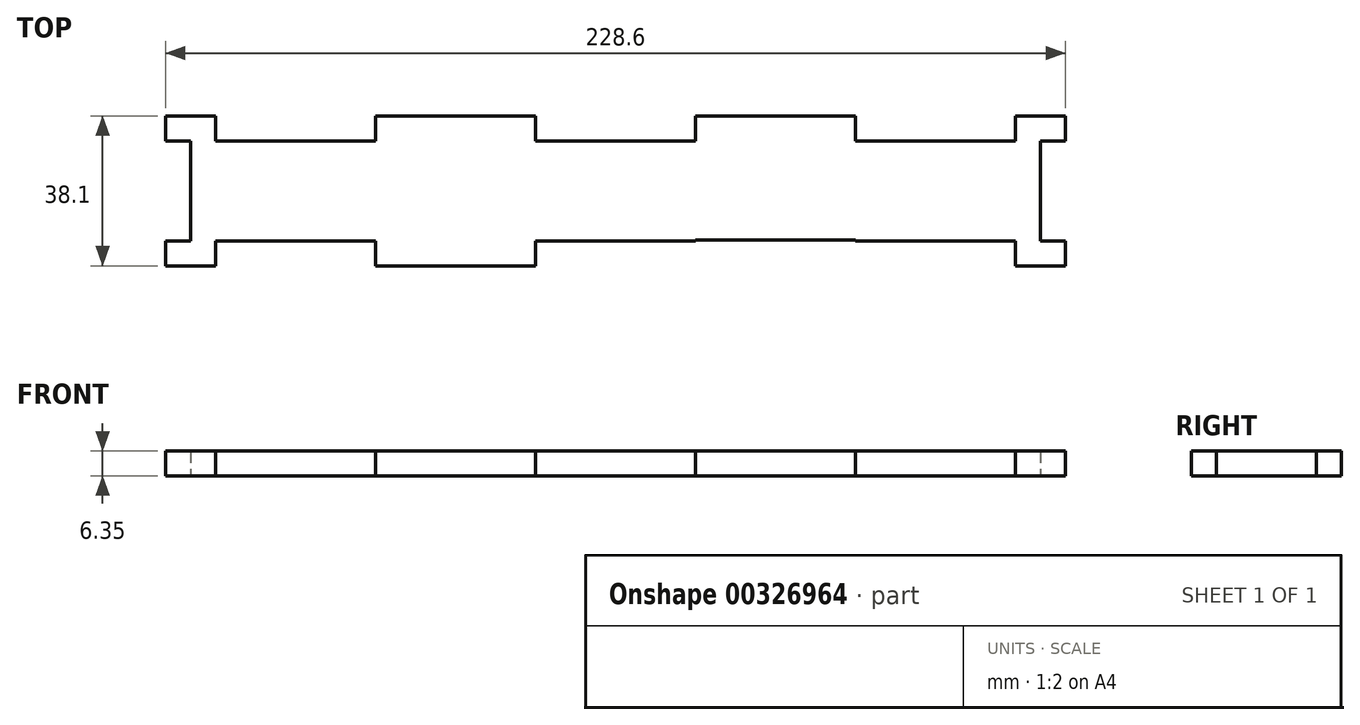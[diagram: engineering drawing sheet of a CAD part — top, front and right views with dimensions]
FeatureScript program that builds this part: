
annotation { "Feature Type Name" : "Feature", "Feature Type Description" : "" }
export const myFeature = defineFeature(function(context is Context, id is Id, definition is map)
    precondition{}
    {
        {
            var Q0;
            Q0=qCreatedBy(makeId("Top.planeOp"),FACE);
            var sketch = newSketch(context, id + "F0", { "sketchPlane" : qUnion([Q0])});
            skLineSegment(sketch, "E0.bottom", {"start": v(-114.3, 19.05) * mm, "end": v(114.3, 19.05) * mm});
            skLineSegment(sketch, "E0.top", {"start": v(-114.3, -19.05) * mm, "end": v(114.3, -19.05) * mm});
            skLineSegment(sketch, "E0.left", {"start": v(-114.3, 19.05) * mm, "end": v(-114.3, -19.05) * mm});
            skLineSegment(sketch, "E0.right", {"start": v(114.3, 19.05) * mm, "end": v(114.3, -19.05) * mm});
            skPoint(sketch, "E0.middle", {"position": v(0, 0) * mm});
            skLineSegment(sketch, "E1", {"start": v(-114.3, 19.05) * mm, "end": v(-114.3, 12.7) * mm});
            skLineSegment(sketch, "E2.bottom", {"start": v(-114.3, 12.7) * mm, "end": v(-107.95, 12.7) * mm});
            skLineSegment(sketch, "E2.top", {"start": v(-114.3, -12.7) * mm, "end": v(-107.95, -12.7) * mm});
            skLineSegment(sketch, "E2.left", {"start": v(-114.3, 12.7) * mm, "end": v(-114.3, -12.7) * mm});
            skLineSegment(sketch, "E2.right", {"start": v(-107.95, 12.7) * mm, "end": v(-107.95, -12.7) * mm});
            skLineSegment(sketch, "E3", {"start": v(-114.3, 19.05) * mm, "end": v(-101.6, 19.05) * mm});
            skLineSegment(sketch, "E4.bottom", {"start": v(-101.6, 19.05) * mm, "end": v(-60.96, 19.05) * mm});
            skLineSegment(sketch, "E4.top", {"start": v(-101.6, 12.7) * mm, "end": v(-60.96, 12.7) * mm});
            skLineSegment(sketch, "E4.left", {"start": v(-101.6, 19.05) * mm, "end": v(-101.6, 12.7) * mm});
            skLineSegment(sketch, "E4.right", {"start": v(-60.96, 19.05) * mm, "end": v(-60.96, 12.7) * mm});
            skLineSegment(sketch, "E5", {"start": v(-60.96, 19.05) * mm, "end": v(-20.32, 19.05) * mm});
            skLineSegment(sketch, "E6.bottom", {"start": v(-20.32, 19.05) * mm, "end": v(20.32, 19.05) * mm});
            skLineSegment(sketch, "E6.top", {"start": v(-20.32, 12.7) * mm, "end": v(20.32, 12.7) * mm});
            skLineSegment(sketch, "E6.left", {"start": v(-20.32, 19.05) * mm, "end": v(-20.32, 12.7) * mm});
            skLineSegment(sketch, "E6.right", {"start": v(20.32, 19.05) * mm, "end": v(20.32, 12.7) * mm});
            skLineSegment(sketch, "E7", {"start": v(20.32, 19.05) * mm, "end": v(38.62, 19.05) * mm});
            skLineSegment(sketch, "E8", {"start": v(114.3, 19.05) * mm, "end": v(101.6, 19.05) * mm});
            skLineSegment(sketch, "E9.bottom", {"start": v(101.6, 19.05) * mm, "end": v(60.96, 19.05) * mm});
            skLineSegment(sketch, "E9.top", {"start": v(101.6, 12.7) * mm, "end": v(60.96, 12.7) * mm});
            skLineSegment(sketch, "E9.left", {"start": v(101.6, 19.05) * mm, "end": v(101.6, 12.7) * mm});
            skLineSegment(sketch, "E9.right", {"start": v(60.96, 19.05) * mm, "end": v(60.96, 12.7) * mm});
            skLineSegment(sketch, "E10", {"start": v(-114.3, -19.05) * mm, "end": v(-101.6, -19.05) * mm});
            skLineSegment(sketch, "E11.bottom", {"start": v(-101.6, -19.05) * mm, "end": v(-60.96, -19.05) * mm});
            skLineSegment(sketch, "E11.top", {"start": v(-101.6, -12.7) * mm, "end": v(-60.96, -12.7) * mm});
            skLineSegment(sketch, "E11.left", {"start": v(-101.6, -19.05) * mm, "end": v(-101.6, -12.7) * mm});
            skLineSegment(sketch, "E11.right", {"start": v(-60.96, -19.05) * mm, "end": v(-60.96, -12.7) * mm});
            skLineSegment(sketch, "E12", {"start": v(-60.96, -19.05) * mm, "end": v(-39.72, -19.05) * mm});
            skLineSegment(sketch, "E13", {"start": v(114.3, -19.05) * mm, "end": v(101.6, -19.05) * mm});
            skLineSegment(sketch, "E14.bottom", {"start": v(101.6, -19.05) * mm, "end": v(60.96, -19.05) * mm});
            skLineSegment(sketch, "E14.top", {"start": v(101.6, -12.7) * mm, "end": v(60.96, -12.7) * mm});
            skLineSegment(sketch, "E14.left", {"start": v(101.6, -19.05) * mm, "end": v(101.6, -12.7) * mm});
            skLineSegment(sketch, "E14.right", {"start": v(60.96, -19.05) * mm, "end": v(60.96, -12.7) * mm});
            skLineSegment(sketch, "E15.bottom", {"start": v(60.96, -19.05) * mm, "end": v(20.32, -19.05) * mm});
            skLineSegment(sketch, "E15.top", {"start": v(60.96, -12.51) * mm, "end": v(20.32, -12.51) * mm});
            skLineSegment(sketch, "E15.left", {"start": v(60.96, -19.05) * mm, "end": v(60.96, -12.51) * mm});
            skLineSegment(sketch, "E15.right", {"start": v(20.32, -19.05) * mm, "end": v(20.32, -12.51) * mm});
            skLineSegment(sketch, "E16.bottom", {"start": v(20.32, -19.05) * mm, "end": v(-20.32, -19.05) * mm});
            skLineSegment(sketch, "E16.top", {"start": v(20.32, -12.7) * mm, "end": v(-20.32, -12.7) * mm});
            skLineSegment(sketch, "E16.left", {"start": v(20.32, -19.05) * mm, "end": v(20.32, -12.7) * mm});
            skLineSegment(sketch, "E16.right", {"start": v(-20.32, -19.05) * mm, "end": v(-20.32, -12.7) * mm});
            skLineSegment(sketch, "E17", {"start": v(114.3, 19.05) * mm, "end": v(114.3, 12.7) * mm});
            skLineSegment(sketch, "E18.bottom", {"start": v(114.3, 12.7) * mm, "end": v(107.95, 12.7) * mm});
            skLineSegment(sketch, "E18.top", {"start": v(114.3, -12.7) * mm, "end": v(107.95, -12.7) * mm});
            skLineSegment(sketch, "E18.left", {"start": v(114.3, 12.7) * mm, "end": v(114.3, -12.7) * mm});
            skLineSegment(sketch, "E18.right", {"start": v(107.95, 12.7) * mm, "end": v(107.95, -12.7) * mm});
            skSolve(sketch);
        }
        {
            var Q0;
            Q0=makeQuery(id+"F0.imprint","IMPRINT",FACE,{"disambiguationData":[TD([[makeQuery(id+"F0.imprint","IMPRINT",EDGE,{"derivedFrom":sQuery(id+"F0.wireOp",EDGE,"E0.bottom")}),-1.0]])]});
            var Q1;
            {var subQ3=sQuery(id+"F0.wireOp",EDGE,"E15.bottom");Q1=makeQuery(id+"F0.imprint","IMPRINT",FACE,{"disambiguationData":[TD([[makeQuery(id+"F0.imprint","IMPRINT",EDGE,{"derivedFrom":subQ3}),-1.0]])]});}
            extrude(context, id + "F1", {"entities" : qUnion([Q0, Q1]), "depth" : 6.35 * mm});
        }
    });
